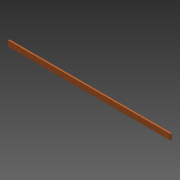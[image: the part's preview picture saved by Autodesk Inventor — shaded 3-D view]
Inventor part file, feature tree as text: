
AUTODESK INVENTOR PART (.ipt)
format: ipt  version: 2013 (Build 170138000, 138)  size: 67,584 bytes
history: native  units: in
note: dims shown in document units (in); Inventor stores cm internally (conversion verified against a paired STEP export)
features: extrude x1, sketch x1
ambient origin geometry x8: Origin, YZ Plane, XZ Plane, XY Plane, X Axis, Y Axis, Z Axis, Center Point
bodies: Solid1 (feature_tree)
feature tree (2):
  extrude  "Extrusion1"  Depth=2.0in
  sketch  "Sketch1"  dims[d0=57.0in d1=2.0in d2=0.5in d3=0.0in]
